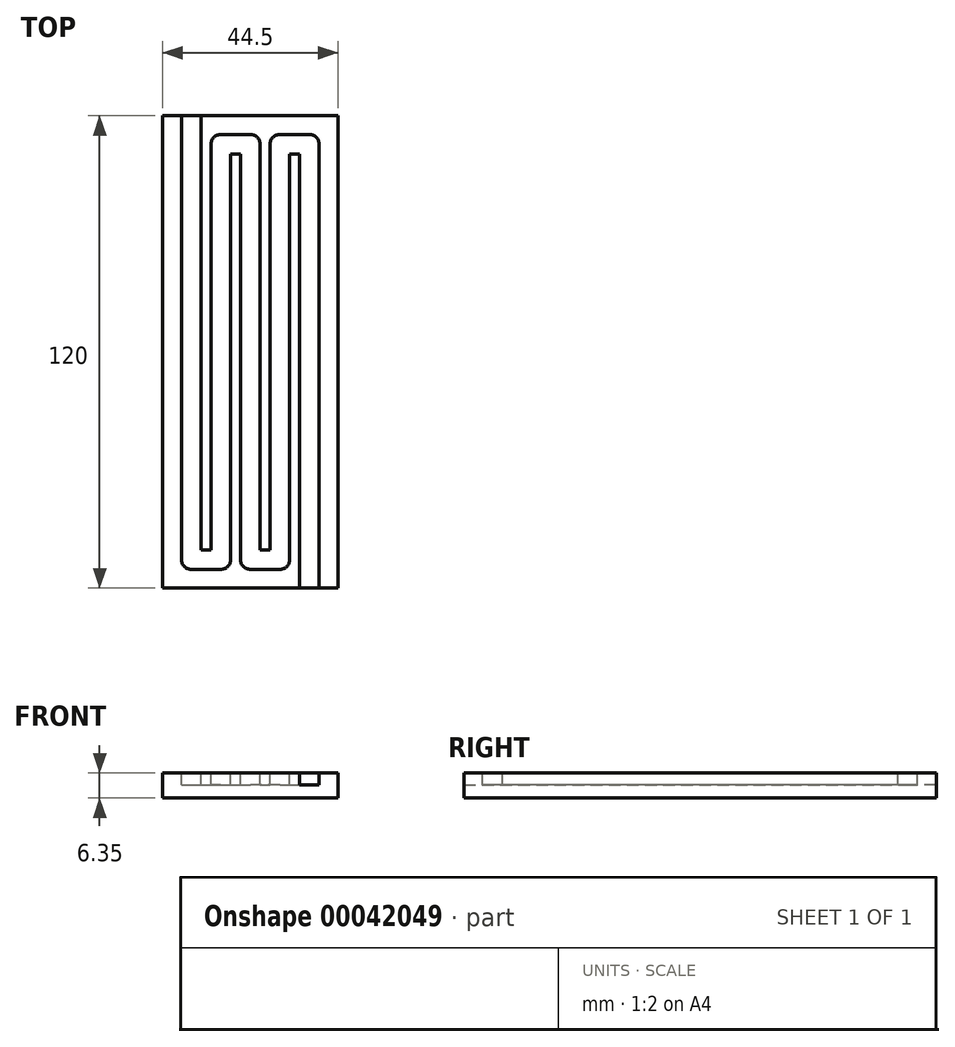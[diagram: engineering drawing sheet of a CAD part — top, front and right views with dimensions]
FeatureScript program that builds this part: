
annotation { "Feature Type Name" : "Feature", "Feature Type Description" : "" }
export const myFeature = defineFeature(function(context is Context, id is Id, definition is map)
    precondition{}
    {
        {
            var Q0;
            Q0=qCreatedBy(makeId("Top.planeOp"),FACE);
            var sketch = newSketch(context, id + "F0", { "sketchPlane" : qUnion([Q0])});
            skLineSegment(sketch, "E0.bottom", {"start": v(-25.1, 86.03) * mm, "end": v(19.4, 86.03) * mm});
            skLineSegment(sketch, "E0.top", {"start": v(-25.1, -33.97) * mm, "end": v(19.4, -33.97) * mm});
            skLineSegment(sketch, "E0.left", {"start": v(-25.1, 86.03) * mm, "end": v(-25.1, -33.97) * mm});
            skLineSegment(sketch, "E0.right", {"start": v(19.4, 86.03) * mm, "end": v(19.4, -33.97) * mm});
            skSolve(sketch);
        }
        {
            var Q0;
            Q0 = qSketchRegion(id + "F0", true);
            extrude(context, id + "F1", {"entities" : qUnion([Q0]), "depth" : 6.35 * mm});
        }
        {
            var Q0;
            Q0=makeQuery(id+"F1.opExtrude","CAP_FACE",FACE,{"disambiguationData":[OSD([sQuery(id+"F0.wireOp",EDGE,"E0.bottom"),sQuery(id+"F0.wireOp",EDGE,"E0.top"),sQuery(id+"F0.wireOp",EDGE,"E0.left"),sQuery(id+"F0.wireOp",EDGE,"E0.right")])],"isStart":false});
            var sketch = newSketch(context, id + "F2", { "sketchPlane" : qUnion([Q0])});
            skLineSegment(sketch, "E1", {"start": v(12.16, -33.97) * mm, "end": v(12.16, 81.28) * mm, "construction": true});
            skLineSegment(sketch, "E2", {"start": v(-17.84, 86.03) * mm, "end": v(-17.84, -29.22) * mm, "construction": true});
            skLineSegment(sketch, "E3.0", {"start": v(9.66, -33.97) * mm, "end": v(9.66, 76.28) * mm});
            skLineSegment(sketch, "E4.0", {"start": v(14.66, -33.97) * mm, "end": v(14.66, 78.78) * mm});
            skLineSegment(sketch, "E5.0", {"start": v(-20.34, 86.03) * mm, "end": v(-20.34, -26.72) * mm});
            skLineSegment(sketch, "E6.0", {"start": v(-15.34, 86.03) * mm, "end": v(-15.34, -24.22) * mm});
            skLineSegment(sketch, "E7.0", {"start": v(-12.84, 78.78) * mm, "end": v(-12.84, -24.22) * mm});
            skLineSegment(sketch, "E8.0", {"start": v(-7.84, 76.28) * mm, "end": v(-7.84, -26.72) * mm});
            skLineSegment(sketch, "E9.0", {"start": v(-10.34, 81.28) * mm, "end": v(-10.34, -29.22) * mm, "construction": true});
            skLineSegment(sketch, "E10.0", {"start": v(-5.34, 76.28) * mm, "end": v(-5.34, -26.72) * mm});
            skLineSegment(sketch, "E11.0", {"start": v(-0.34, 78.78) * mm, "end": v(-0.34, -24.22) * mm});
            skLineSegment(sketch, "E12.0", {"start": v(-2.84, 81.28) * mm, "end": v(-2.84, -29.22) * mm, "construction": true});
            skLineSegment(sketch, "E13.0", {"start": v(2.16, 78.78) * mm, "end": v(2.16, -24.22) * mm});
            skLineSegment(sketch, "E14.0", {"start": v(7.16, 76.28) * mm, "end": v(7.16, -26.72) * mm});
            skLineSegment(sketch, "E15.0", {"start": v(4.66, 81.28) * mm, "end": v(4.66, -29.22) * mm, "construction": true});
            skLineSegment(sketch, "E16.trimOffspring", {"start": v(-15.34, -24.22) * mm, "end": v(-12.84, -24.22) * mm});
            skLineSegment(sketch, "E17", {"start": v(-17.84, -29.22) * mm, "end": v(-10.34, -29.22) * mm});
            skLineSegment(sketch, "E18", {"start": v(-10.34, 81.28) * mm, "end": v(-2.84, 81.28) * mm});
            skLineSegment(sketch, "E19.trimOffspring", {"start": v(-7.84, 76.28) * mm, "end": v(-5.34, 76.28) * mm});
            skLineSegment(sketch, "E20", {"start": v(4.66, 81.28) * mm, "end": v(12.16, 81.28) * mm});
            skLineSegment(sketch, "E21.trimOffspring", {"start": v(7.16, 76.28) * mm, "end": v(9.66, 76.28) * mm});
            skLineSegment(sketch, "E22.trimOffspring", {"start": v(14.66, 76.28) * mm, "end": v(30.35, 76.28) * mm});
            skLineSegment(sketch, "E23", {"start": v(4.66, -29.22) * mm, "end": v(-2.84, -29.22) * mm});
            skLineSegment(sketch, "E24.trimOffspring", {"start": v(-0.34, -24.22) * mm, "end": v(2.16, -24.22) * mm});
            skPoint(sketch, "E25.visualSharp", {"position": v(14.66, 81.28) * mm});
            skArc(sketch, "E25.filletArc", {"start": v(14.66, 78.78) * mm, "mid": v(13.93, 80.55) * mm, "end": v(12.16, 81.28) * mm});
            skPoint(sketch, "E26.visualSharp", {"position": v(2.16, 81.28) * mm});
            skArc(sketch, "E26.filletArc", {"start": v(4.66, 81.28) * mm, "mid": v(2.9, 80.55) * mm, "end": v(2.16, 78.78) * mm});
            skPoint(sketch, "E27.visualSharp", {"position": v(-0.34, 81.28) * mm});
            skArc(sketch, "E27.filletArc", {"start": v(-0.34, 78.78) * mm, "mid": v(-1.07, 80.55) * mm, "end": v(-2.84, 81.28) * mm});
            skPoint(sketch, "E28.visualSharp", {"position": v(-12.84, 81.28) * mm});
            skArc(sketch, "E28.filletArc", {"start": v(-10.34, 81.28) * mm, "mid": v(-12.1, 80.55) * mm, "end": v(-12.84, 78.78) * mm});
            skPoint(sketch, "E29.visualSharp", {"position": v(7.16, -29.22) * mm});
            skArc(sketch, "E29.filletArc", {"start": v(4.66, -29.22) * mm, "mid": v(6.43, -28.49) * mm, "end": v(7.16, -26.72) * mm});
            skPoint(sketch, "E30.visualSharp", {"position": v(-5.34, -29.22) * mm});
            skArc(sketch, "E30.filletArc", {"start": v(-5.34, -26.72) * mm, "mid": v(-4.6, -28.49) * mm, "end": v(-2.84, -29.22) * mm});
            skPoint(sketch, "E31.visualSharp", {"position": v(-7.84, -29.22) * mm});
            skArc(sketch, "E31.filletArc", {"start": v(-10.34, -29.22) * mm, "mid": v(-8.57, -28.49) * mm, "end": v(-7.84, -26.72) * mm});
            skPoint(sketch, "E32.visualSharp", {"position": v(-20.34, -29.22) * mm});
            skArc(sketch, "E32.filletArc", {"start": v(-20.34, -26.72) * mm, "mid": v(-19.6, -28.49) * mm, "end": v(-17.84, -29.22) * mm});
            skSolve(sketch);
        }
        {
            var Q0;
            {var subQ0=sQuery(id+"F2.wireOp",EDGE,"E3.0");Q0=makeQuery(id+"F2.imprint","IMPRINT",FACE,{"disambiguationData":[TD([[makeQuery(id+"F2.imprint","IMPRINT",EDGE,{"derivedFrom":subQ0}),-1.0]])]});}
            extrude(context, id + "F3", {"entities" : qUnion([Q0]), "operationType" : NewBodyOperationType.REMOVE, "oppositeDirection" : true, "depth" : 3 * mm});
        }
    });
